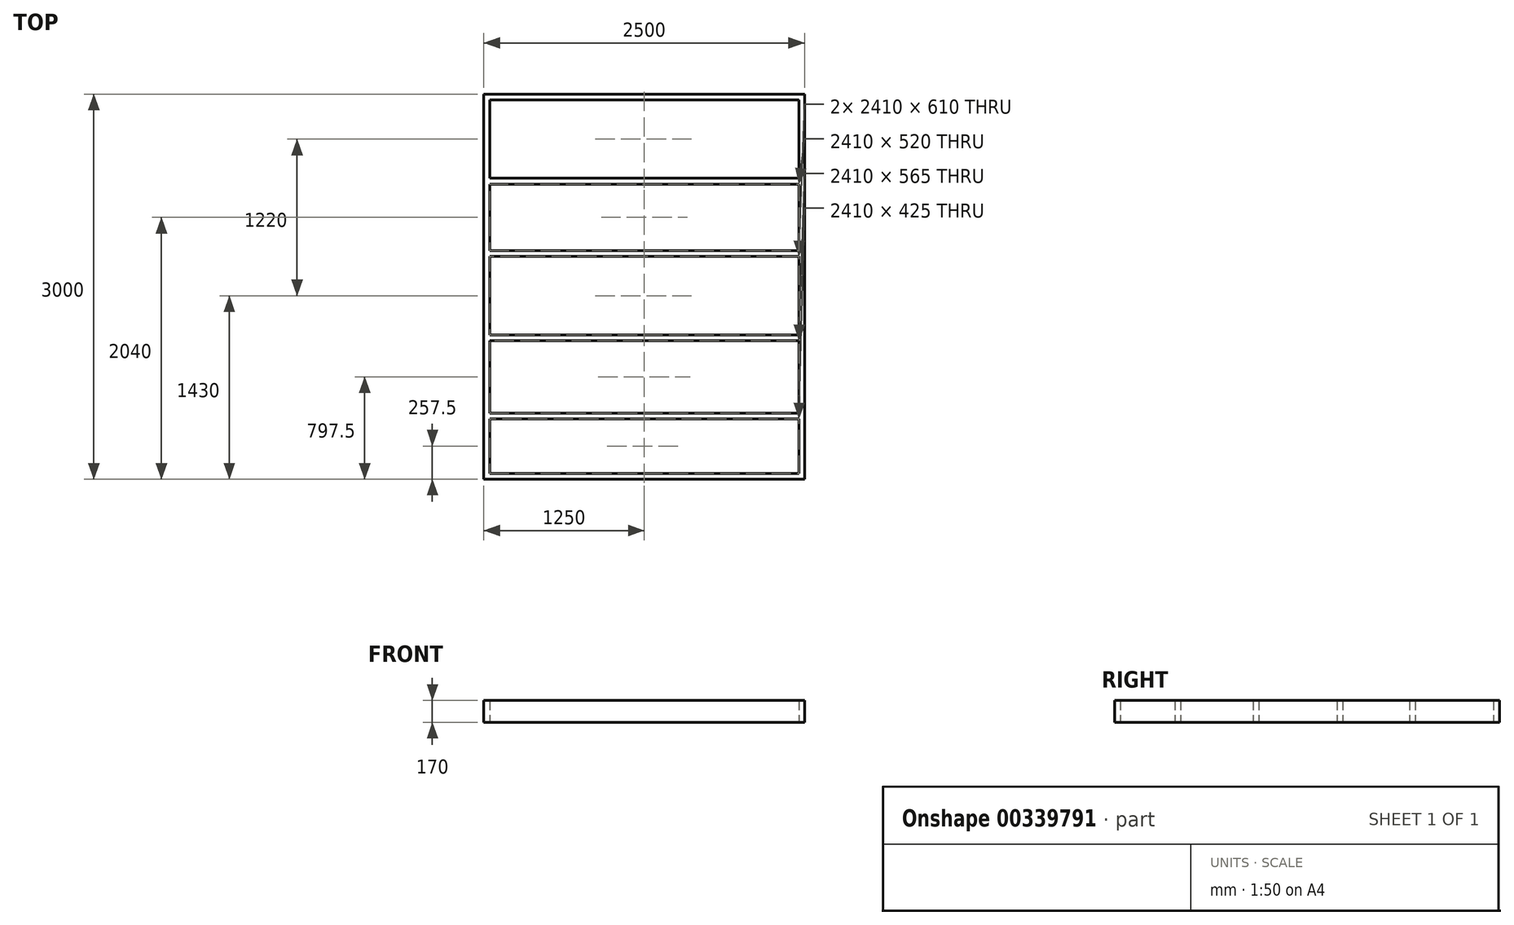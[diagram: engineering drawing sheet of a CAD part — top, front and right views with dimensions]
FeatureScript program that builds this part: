
annotation { "Feature Type Name" : "Feature", "Feature Type Description" : "" }
export const myFeature = defineFeature(function(context is Context, id is Id, definition is map)
    precondition{}
    {
        {
            var Q0;
            Q0=qCreatedBy(makeId("Top.planeOp"),FACE);
            var sketch = newSketch(context, id + "F0", { "sketchPlane" : qUnion([Q0])});
            skLineSegment(sketch, "E0.bottom", {"start": v(0, 0) * mm, "end": v(2500, 0) * mm});
            skLineSegment(sketch, "E0.top", {"start": v(0, 3000) * mm, "end": v(2500, 3000) * mm});
            skLineSegment(sketch, "E1.0", {"start": v(45, 2955) * mm, "end": v(2455, 2955) * mm});
            skLineSegment(sketch, "E1.1", {"start": v(45, 45) * mm, "end": v(45, 470) * mm});
            skLineSegment(sketch, "E1.2", {"start": v(45, 45) * mm, "end": v(2455, 45) * mm});
            skLineSegment(sketch, "E1.3", {"start": v(2455, 45) * mm, "end": v(2455, 470) * mm});
            skLineSegment(sketch, "E2", {"start": v(45, 2345) * mm, "end": v(2455, 2345) * mm});
            skLineSegment(sketch, "E3", {"start": v(2455, 1780) * mm, "end": v(45, 1780) * mm});
            skLineSegment(sketch, "E4", {"start": v(45, 1125) * mm, "end": v(2455, 1125) * mm});
            skLineSegment(sketch, "E5", {"start": v(2455, 515) * mm, "end": v(45, 515) * mm});
            skLineSegment(sketch, "E6", {"start": v(2500, 3000) * mm, "end": v(2500, 0) * mm});
            skLineSegment(sketch, "E7", {"start": v(0, 0) * mm, "end": v(0, 3000) * mm});
            skLineSegment(sketch, "E8.0", {"start": v(45, 2300) * mm, "end": v(2455, 2300) * mm});
            skLineSegment(sketch, "E9.0", {"start": v(2455, 1735) * mm, "end": v(45, 1735) * mm});
            skLineSegment(sketch, "E10.0", {"start": v(45, 1080) * mm, "end": v(2455, 1080) * mm});
            skLineSegment(sketch, "E11.0", {"start": v(2455, 470) * mm, "end": v(45, 470) * mm});
            skLineSegment(sketch, "E12.trimOffspring", {"start": v(45, 2345) * mm, "end": v(45, 2955) * mm});
            skLineSegment(sketch, "E13.trimOffspring", {"start": v(2455, 2345) * mm, "end": v(2455, 2955) * mm});
            skPoint(sketch, "E14.orphan", {"position": v(2500, 2345) * mm});
            skLineSegment(sketch, "E15.trimOffspring", {"start": v(2455, 1780) * mm, "end": v(2455, 2300) * mm});
            skLineSegment(sketch, "E16.trimOffspring", {"start": v(45, 1780) * mm, "end": v(45, 2300) * mm});
            skPoint(sketch, "E17.orphan", {"position": v(0, 1780) * mm});
            skLineSegment(sketch, "E18.trimOffspring", {"start": v(45, 1125) * mm, "end": v(45, 1735) * mm});
            skPoint(sketch, "E19.orphan", {"position": v(2500, 1125) * mm});
            skLineSegment(sketch, "E20.trimOffspring", {"start": v(2455, 1125) * mm, "end": v(2455, 1735) * mm});
            skLineSegment(sketch, "E21.trimOffspring", {"start": v(45, 515) * mm, "end": v(45, 1080) * mm});
            skLineSegment(sketch, "E22.trimOffspring", {"start": v(2455, 515) * mm, "end": v(2455, 1080) * mm});
            skSolve(sketch);
        }
        {
            var Q0;
            Q0=makeQuery(id+"F0.imprint","IMPRINT",FACE,{"disambiguationData":[TD([[makeQuery(id+"F0.imprint","IMPRINT",EDGE,{"derivedFrom":sQuery(id+"F0.wireOp",EDGE,"E0.bottom")}),1.0]])]});
            extrude(context, id + "F1", {"entities" : qUnion([Q0]), "depth" : 170 * mm});
        }
    });
